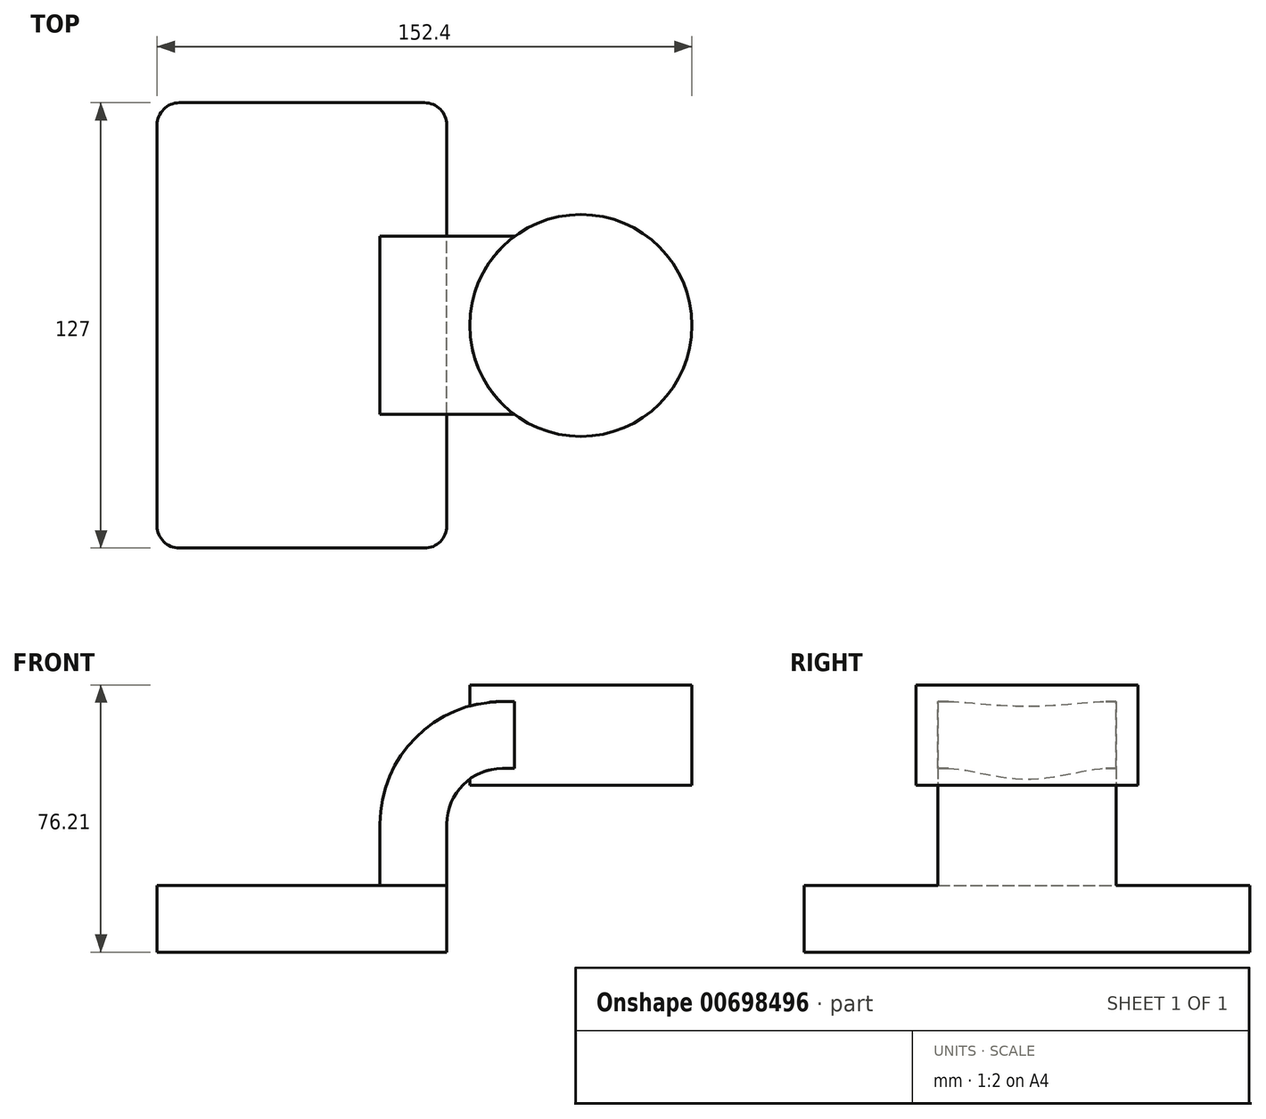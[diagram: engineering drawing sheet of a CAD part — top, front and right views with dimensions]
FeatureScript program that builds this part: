
annotation { "Feature Type Name" : "Feature", "Feature Type Description" : "" }
export const myFeature = defineFeature(function(context is Context, id is Id, definition is map)
    precondition{}
    {
        {
            var Q0;
            Q0=qCreatedBy(makeId("Front.planeOp"),FACE);
            var sketch = newSketch(context, id + "F0", { "sketchPlane" : qUnion([Q0])});
            skLineSegment(sketch, "E0.bottom", {"start": v(-41.28, 9.52) * mm, "end": v(41.28, 9.53) * mm});
            skLineSegment(sketch, "E0.top", {"start": v(-41.28, -9.53) * mm, "end": v(41.28, -9.53) * mm});
            skLineSegment(sketch, "E0.left", {"start": v(-41.28, 9.52) * mm, "end": v(-41.28, -9.53) * mm});
            skLineSegment(sketch, "E0.right", {"start": v(41.28, 9.53) * mm, "end": v(41.28, -9.52) * mm});
            skPoint(sketch, "E0.middle", {"position": v(0, 0) * mm});
            skLineSegment(sketch, "E1.bottom", {"start": v(60.33, 66.68) * mm, "end": v(111.12, 66.68) * mm});
            skLineSegment(sketch, "E1.top", {"start": v(60.33, 38.1) * mm, "end": v(111.12, 38.1) * mm});
            skLineSegment(sketch, "E1.left", {"start": v(60.33, 66.68) * mm, "end": v(60.33, 38.1) * mm});
            skLineSegment(sketch, "E1.right", {"start": v(111.12, 66.68) * mm, "end": v(111.12, 38.1) * mm});
            skPoint(sketch, "E1.middle", {"position": v(85.72, 52.39) * mm});
            skLineSegment(sketch, "E2", {"start": v(41.27, 9.53) * mm, "end": v(41.27, 26.98) * mm});
            skArc(sketch, "E3", {"start": v(41.27, 26.98) * mm, "mid": v(45.92, 38.2) * mm, "end": v(57.15, 42.86) * mm});
            skPoint(sketch, "E4.endSnap0", {"position": v(45.92, 38.2) * mm});
            skLineSegment(sketch, "E5", {"start": v(57.15, 42.86) * mm, "end": v(79.47, 42.86) * mm});
            skLineSegment(sketch, "E6.0", {"start": v(57.15, 61.9) * mm, "end": v(79.47, 61.9) * mm});
            skArc(sketch, "E6.1", {"start": v(22.22, 26.98) * mm, "mid": v(32.45, 51.68) * mm, "end": v(57.15, 61.9) * mm});
            skLineSegment(sketch, "E6.2", {"start": v(22.22, 9.53) * mm, "end": v(22.22, 26.98) * mm});
            skFitSpline(sketch, "E7", {"points": [v(-41.28, 9.52) * mm, v(57.15, 61.9) * mm], "startDerivative": vector(33.1, 94.26) * mm, "endDerivative": vector(85.28, -9.98) * mm});
            skLineSegment(sketch, "E8", {"start": v(79.47, 38.1) * mm, "end": v(79.47, 42.86) * mm});
            skLineSegment(sketch, "E9", {"start": v(79.47, 61.9) * mm, "end": v(79.47, 66.68) * mm});
            skLineSegment(sketch, "E10", {"start": v(79.47, 66.68) * mm, "end": v(79.47, 61.9) * mm});
            skLineSegment(sketch, "E11", {"start": v(79.47, 61.9) * mm, "end": v(79.47, 42.86) * mm});
            skSolve(sketch);
        }
        {
            var Q0;
            Q0=makeQuery(id+"F0.imprint","IMPRINT",FACE,{"disambiguationData":[TD([[makeQuery(id+"F0.imprint","IMPRINT",EDGE,{"derivedFrom":sQuery(id+"F0.wireOp",EDGE,"E0.top")}),1.0]])]});
            extrude(context, id + "F1", {"entities" : qUnion([Q0]), "endBound" : BoundingType.SYMMETRIC, "depth" : 127 * mm, "offsetDistance" : 25.4 * mm});
        }
        {
            var Q0;
            {var subQ5=sQuery(id+"F0.wireOp",EDGE,"E11");Q0=makeQuery(id+"F0.imprint","IMPRINT",FACE,{"disambiguationData":[TD([[makeQuery(id+"F0.imprint","IMPRINT",EDGE,{"derivedFrom":subQ5}),-1.0]])]});}
            var Q1;
            {var subQ1=sQuery(id+"F0.wireOp",EDGE,"E2");Q1=makeQuery(id+"F0.imprint","IMPRINT",FACE,{"disambiguationData":[TD([[makeQuery(id+"F0.imprint","IMPRINT",EDGE,{"derivedFrom":subQ1}),1.0]])]});}
            extrude(context, id + "F2", {"entities" : qUnion([Q0, Q1]), "operationType" : NewBodyOperationType.ADD, "endBound" : BoundingType.SYMMETRIC, "depth" : 50.8 * mm, "offsetDistance" : 25.4 * mm});
        }
        {
            var Q0;
            Q0=makeQuery(id+"F0.imprint","IMPRINT",FACE,{"disambiguationData":[TD([[makeQuery(id+"F0.imprint","IMPRINT",EDGE,{"derivedFrom":sQuery(id+"F0.wireOp",EDGE,"E6.1")}),1.0]])]});
            extrude(context, id + "F3", {"entities" : qUnion([Q0]), "operationType" : NewBodyOperationType.ADD, "endBound" : BoundingType.SYMMETRIC, "depth" : 15.88 * mm, "offsetDistance" : 25.4 * mm});
        }
        {
            var Q0;
            {var subQ1=sQuery(id+"F0.wireOp",EDGE,"E1.right");Q0=makeQuery(id+"F0.imprint","IMPRINT",FACE,{"disambiguationData":[TD([[makeQuery(id+"F0.imprint","IMPRINT",EDGE,{"derivedFrom":subQ1}),-1.0]])]});}
            var Q1;
            Q1=sQuery(id+"F0.wireOp",EDGE,"E11");
            revolve(context, id + "F4", {"operationType" : NewBodyOperationType.ADD, "entities" : qUnion([Q0]), "axis" : qUnion([Q1]), "revolveType" : RevolveType.FULL});
        }
        {
            var Q0;
            Q0=makeQuery(id+"F1.opExtrude","CAP_EDGE",EDGE,{"disambiguationData":[OSD([sQuery(id+"F0.wireOp",EDGE,"E0.left")])],"isStart":false});
            var Q1;
            Q1=makeQuery(id+"F1.opExtrude","CAP_EDGE",EDGE,{"disambiguationData":[OSD([sQuery(id+"F0.wireOp",EDGE,"E0.right")])],"isStart":false});
            var Q2;
            Q2=makeQuery(id+"F1.opExtrude","CAP_EDGE",EDGE,{"disambiguationData":[OSD([sQuery(id+"F0.wireOp",EDGE,"E0.left")])],"isStart":true});
            var Q3;
            Q3=makeQuery(id+"F1.opExtrude","CAP_EDGE",EDGE,{"disambiguationData":[OSD([sQuery(id+"F0.wireOp",EDGE,"E0.right")])],"isStart":true});
            fillet(context, id + "F5", {"entities" : qUnion([Q0, Q1, Q2, Q3]), "radius" : 6.35 * mm, "tangentPropagation" : true, "allowEdgeOverflow" : false});
        }
    });
